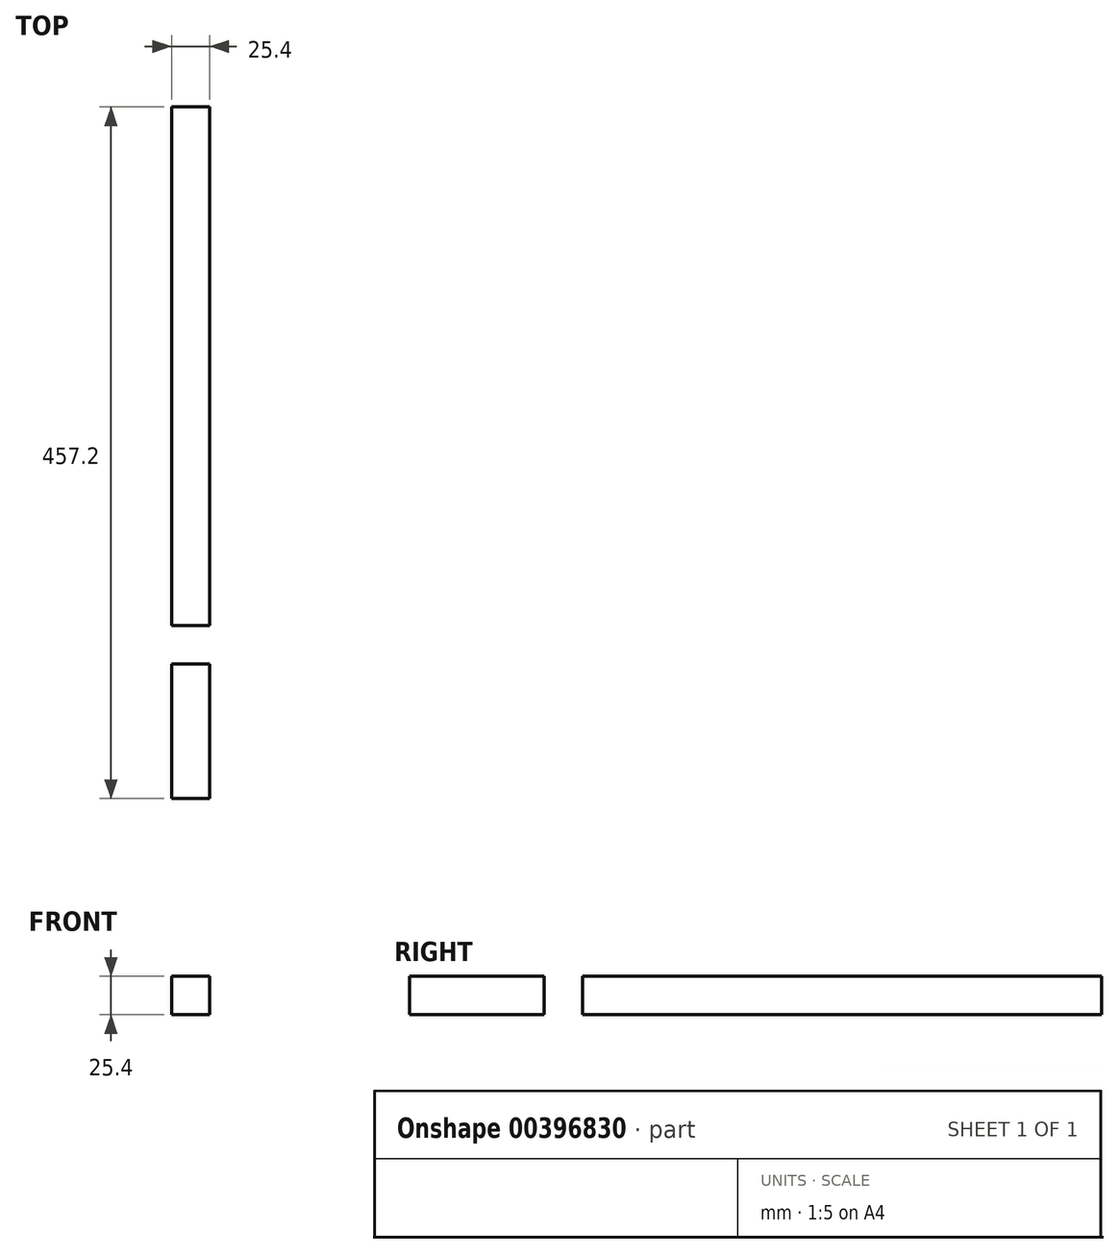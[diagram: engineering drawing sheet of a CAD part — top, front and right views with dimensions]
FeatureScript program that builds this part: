
annotation { "Feature Type Name" : "Feature", "Feature Type Description" : "" }
export const myFeature = defineFeature(function(context is Context, id is Id, definition is map)
    precondition{}
    {
        {
            var Q0;
            Q0=qCreatedBy(makeId("Top.planeOp"),FACE);
            var sketch = newSketch(context, id + "F0", { "sketchPlane" : qUnion([Q0])});
            skLineSegment(sketch, "E0.bottom", {"start": v(12.7, 228.6) * mm, "end": v(-12.7, 228.6) * mm});
            skLineSegment(sketch, "E0.top", {"start": v(12.7, -228.6) * mm, "end": v(-12.7, -228.6) * mm});
            skLineSegment(sketch, "E0.left", {"start": v(12.7, 228.6) * mm, "end": v(12.7, -228.6) * mm});
            skLineSegment(sketch, "E0.right", {"start": v(-12.7, 228.6) * mm, "end": v(-12.7, -228.6) * mm});
            skPoint(sketch, "E0.middle", {"position": v(0, 0) * mm});
            skSolve(sketch);
        }
        {
            var Q0;
            Q0=makeQuery(id+"F0.imprint","IMPRINT",FACE,{"disambiguationData":[TD([[makeQuery(id+"F0.imprint","IMPRINT",EDGE,{"derivedFrom":sQuery(id+"F0.wireOp",EDGE,"E0.bottom")}),1.0]])]});
            extrude(context, id + "F1", {"entities" : qUnion([Q0]), "depth" : 25.4 * mm});
        }
        {
            var Q0;
            Q0=makeQuery(id+"F1.opExtrude","CAP_FACE",FACE,{"disambiguationData":[OSD([sQuery(id+"F0.wireOp",EDGE,"E0.bottom"),sQuery(id+"F0.wireOp",EDGE,"E0.top"),sQuery(id+"F0.wireOp",EDGE,"E0.left"),sQuery(id+"F0.wireOp",EDGE,"E0.right")])],"isStart":false});
            var sketch = newSketch(context, id + "F2", { "sketchPlane" : qUnion([Q0])});
            skLineSegment(sketch, "E1", {"start": v(0, 0) * mm, "end": v(0, -228.6) * mm});
            skLineSegment(sketch, "E2", {"start": v(12.7, 0) * mm, "end": v(12.7, -114.3) * mm});
            skLineSegment(sketch, "E3.bottom", {"start": v(12.7, -114.3) * mm, "end": v(-12.7, -114.3) * mm});
            skLineSegment(sketch, "E3.top", {"start": v(12.7, -139.7) * mm, "end": v(-12.7, -139.7) * mm});
            skLineSegment(sketch, "E3.left", {"start": v(12.7, -114.3) * mm, "end": v(12.7, -139.7) * mm});
            skLineSegment(sketch, "E3.right", {"start": v(-12.7, -114.3) * mm, "end": v(-12.7, -139.7) * mm});
            skSolve(sketch);
        }
        {
            var Q0;
            {var subQ5=sQuery(id+"F2.wireOp",EDGE,"E3.left");Q0=makeQuery(id+"F2.imprint","IMPRINT",FACE,{"disambiguationData":[TD([[makeQuery(id+"F2.imprint","IMPRINT",EDGE,{"derivedFrom":subQ5}),-1.0]])]});}
            var Q1;
            {var subQ5=sQuery(id+"F2.wireOp",EDGE,"E3.right");Q1=makeQuery(id+"F2.imprint","IMPRINT",FACE,{"disambiguationData":[TD([[makeQuery(id+"F2.imprint","IMPRINT",EDGE,{"derivedFrom":subQ5}),1.0]])]});}
            extrude(context, id + "F3", {"entities" : qUnion([Q0, Q1]), "operationType" : NewBodyOperationType.REMOVE, "oppositeDirection" : true, "depth" : 25.4 * mm});
        }
    });
